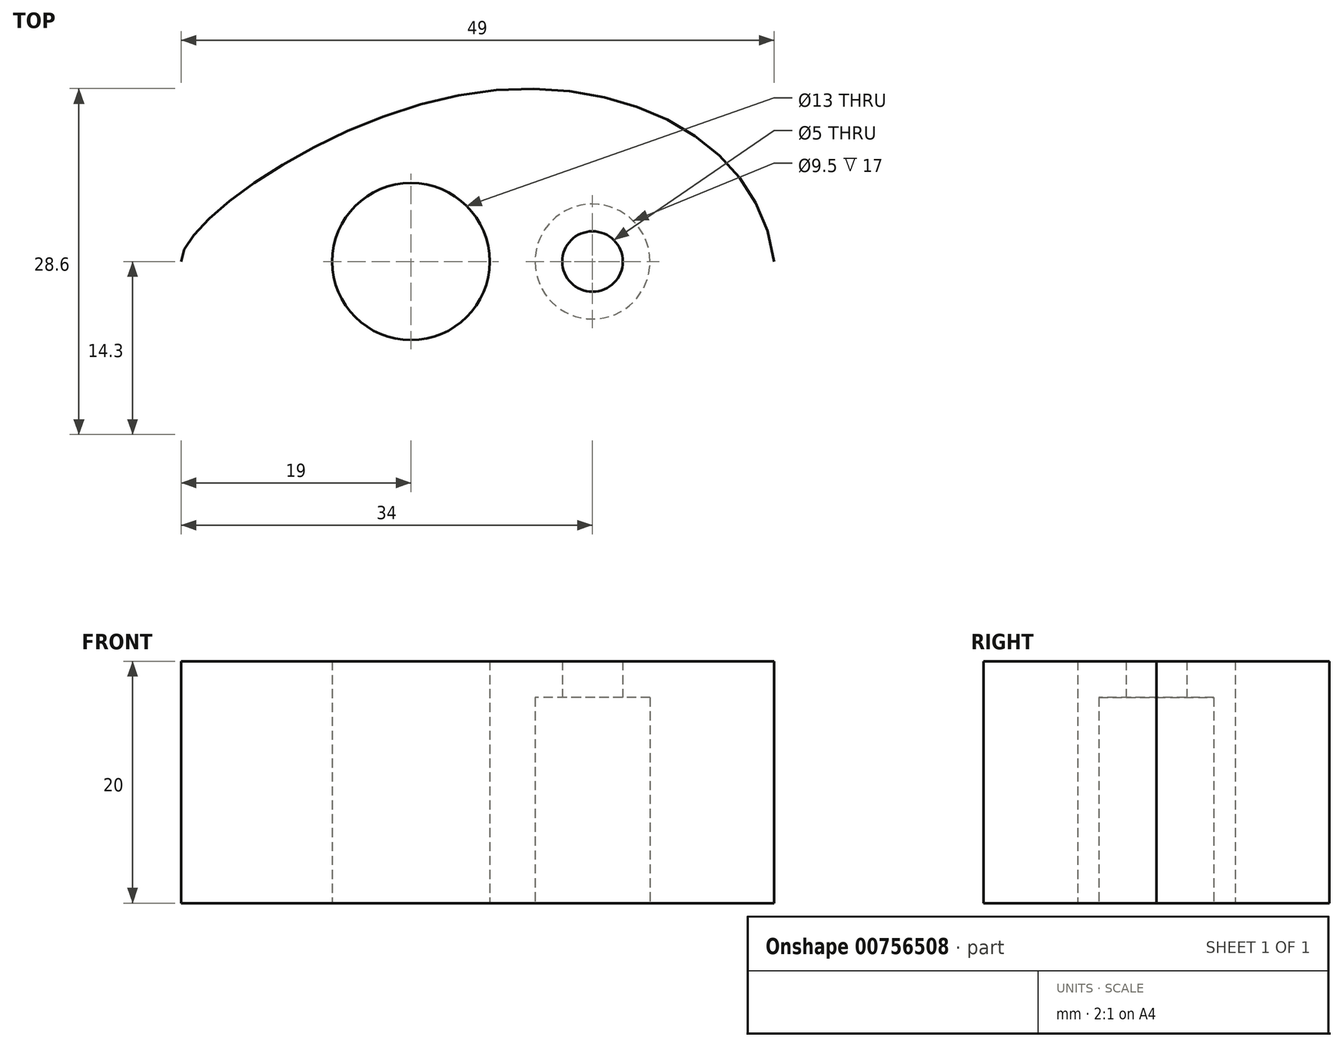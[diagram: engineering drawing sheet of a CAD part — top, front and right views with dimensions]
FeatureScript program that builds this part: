
annotation { "Feature Type Name" : "Feature", "Feature Type Description" : "" }
export const myFeature = defineFeature(function(context is Context, id is Id, definition is map)
    precondition{}
    {
        {
            var Q0;
            Q0=qCreatedBy(makeId("Top.planeOp"),FACE);
            var sketch = newSketch(context, id + "F0", { "sketchPlane" : qUnion([Q0])});
            skFitSpline(sketch, "E0", {"points": [v(-34, 0) * mm, v(-9.5, 14) * mm, v(15, 0) * mm], "startDerivative": vector(-0.01, 20.2) * mm, "endDerivative": vector(7.4, -60.56) * mm});
            skArc(sketch, "E1", {"start": v(-21.5, 0) * mm, "mid": v(-15, 6.5) * mm, "end": v(-8.5, 0) * mm});
            skPoint(sketch, "E1.startSnap0", {"position": v(-17, 0) * mm});
            skLineSegment(sketch, "E2", {"start": v(-34, 0) * mm, "end": v(-21.5, 0) * mm});
            skArc(sketch, "E3", {"start": v(-2.5, 0) * mm, "mid": v(0, 2.5) * mm, "end": v(2.5, 0) * mm});
            skLineSegment(sketch, "E4", {"start": v(-8.5, 0) * mm, "end": v(-2.5, 0) * mm});
            skLineSegment(sketch, "E5", {"start": v(2.5, 0) * mm, "end": v(15, 0) * mm});
            skSolve(sketch);
        }
        {
            var Q0;
            Q0 = qSketchRegion(id + "F0", true);
            extrude(context, id + "F1", {"entities" : qUnion([Q0]), "depth" : 20 * mm, "offsetDistance" : 25 * mm});
        }
        {
            var Q0;
            Q0=makeQuery(id+"F1.opExtrude","SWEPT_BODY",BODY,{"disambiguationData":[OSD([sQuery(id+"F0.wireOp",EDGE,"E0"),sQuery(id+"F0.wireOp",EDGE,"E1"),sQuery(id+"F0.wireOp",EDGE,"McHGNHOU-62kw-HZgm-CWgZ-VDhnGf6BRuoS"),sQuery(id+"F0.wireOp",EDGE,"E2"),sQuery(id+"F0.wireOp",EDGE,"D958tiaN-heJL-5NL5-mns3-F5RS8ibdN3Pm"),sQuery(id+"F0.wireOp",EDGE,"xE7LKnkU-Hi0Y-gHIj-jbuS-JquG0hnZopf2")])]});
            var Q1;
            Q1=qCreatedBy(makeId("Front.planeOp"),FACE);
            mirror(context, id + "F2", {"operationType" : NewBodyOperationType.ADD, "entities" : qUnion([Q0]), "mirrorPlane" : qUnion([Q1])});
        }
        {
            var Q0;
            Q0=qCreatedBy(makeId("Top.planeOp"),FACE);
            var sketch = newSketch(context, id + "F3", { "sketchPlane" : qUnion([Q0])});
            skLineSegment(sketch, "E6", {"start": v(0, 0) * mm, "end": v(-15, 0) * mm});
            skCircle(sketch, "E7", {"center": v(-15, 0) * mm, "radius": 6.5 * mm});
            skCircle(sketch, "E8", {"center": v(-15, 0) * mm, "radius": 6.8 * mm});
            skSolve(sketch);
        }
        {
            var Q0;
            Q0 = qSketchRegion(id + "F3", true);
            extrude(context, id + "F4", {"entities" : qUnion([Q0]), "operationType" : NewBodyOperationType.ADD, "depth" : 20 * mm, "offsetDistance" : 25 * mm});
        }
        {
            var Q0;
            Q0=qCreatedBy(makeId("Top.planeOp"),FACE);
            var sketch = newSketch(context, id + "F5", { "sketchPlane" : qUnion([Q0])});
            skCircle(sketch, "E9", {"center": v(0, 0) * mm, "radius": 4.75 * mm});
            skSolve(sketch);
        }
        {
            var Q0;
            Q0 = qSketchRegion(id + "F5", true);
            extrude(context, id + "F6", {"entities" : qUnion([Q0]), "depth" : 17 * mm, "offsetDistance" : 25 * mm});
        }
        {
            var Q0;
            Q0=makeQuery(id+"F6.opExtrude","SWEPT_BODY",BODY,{"disambiguationData":[OSD([sQuery(id+"F5.wireOp",EDGE,"E9")])]});
            var Q1;
            Q1=makeQuery(id+"F1.opExtrude","SWEPT_BODY",BODY,{"disambiguationData":[OSD([sQuery(id+"F0.wireOp",EDGE,"E0"),sQuery(id+"F0.wireOp",EDGE,"E1"),sQuery(id+"F0.wireOp",EDGE,"McHGNHOU-62kw-HZgm-CWgZ-VDhnGf6BRuoS"),sQuery(id+"F0.wireOp",EDGE,"E2"),sQuery(id+"F0.wireOp",EDGE,"D958tiaN-heJL-5NL5-mns3-F5RS8ibdN3Pm"),sQuery(id+"F0.wireOp",EDGE,"xE7LKnkU-Hi0Y-gHIj-jbuS-JquG0hnZopf2")])]});
            booleanBodies(context, id + "F7", {"operationType" : BooleanOperationType.SUBTRACTION, "tools" : qUnion([Q0]), "targets" : qUnion([Q1])});
        }
    });
